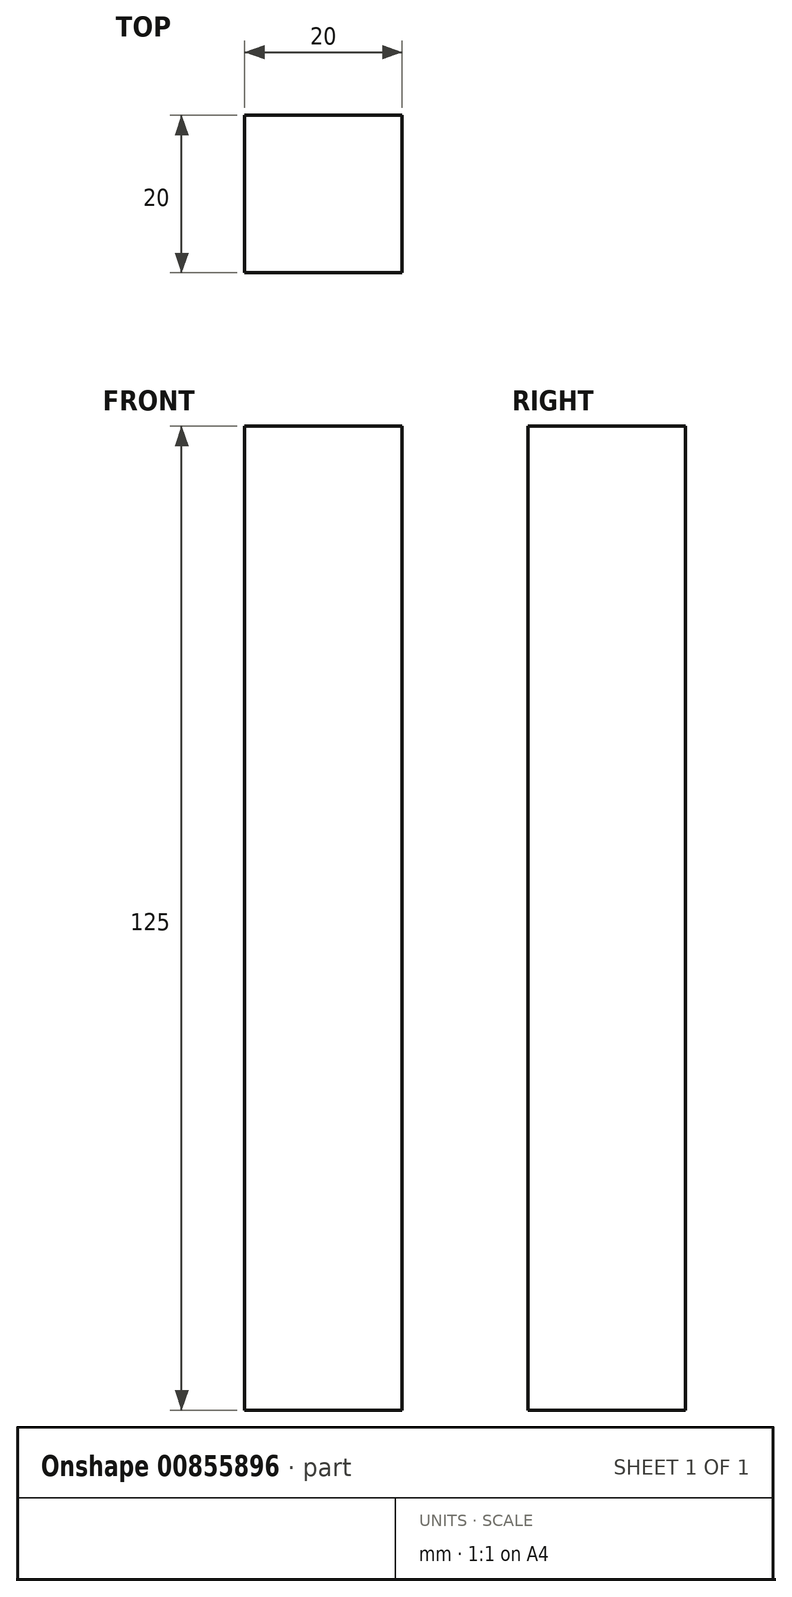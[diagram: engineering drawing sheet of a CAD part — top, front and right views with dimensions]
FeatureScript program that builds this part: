
annotation { "Feature Type Name" : "Feature", "Feature Type Description" : "" }
export const myFeature = defineFeature(function(context is Context, id is Id, definition is map)
    precondition{}
    {
        {
            var Q0;
            Q0=qCreatedBy(makeId("Top.planeOp"),FACE);
            var sketch = newSketch(context, id + "F0", { "sketchPlane" : qUnion([Q0])});
            skLineSegment(sketch, "E0.bottom", {"start": v(0, 0) * mm, "end": v(-20, 0) * mm});
            skLineSegment(sketch, "E0.top", {"start": v(0, 20) * mm, "end": v(-20, 20) * mm});
            skLineSegment(sketch, "E0.left", {"start": v(0, 0) * mm, "end": v(0, 20) * mm});
            skLineSegment(sketch, "E0.right", {"start": v(-20, 0) * mm, "end": v(-20, 20) * mm});
            skSolve(sketch);
        }
        {
            var Q0;
            Q0=makeQuery(id+"F0.imprint","IMPRINT",FACE,{"disambiguationData":[TD([[makeQuery(id+"F0.imprint","IMPRINT",EDGE,{"derivedFrom":sQuery(id+"F0.wireOp",EDGE,"E0.bottom")}),-1.0]])]});
            extrude(context, id + "F1", {"entities" : qUnion([Q0]), "depth" : 125 * mm, "offsetDistance" : 25 * mm});
        }
    });
